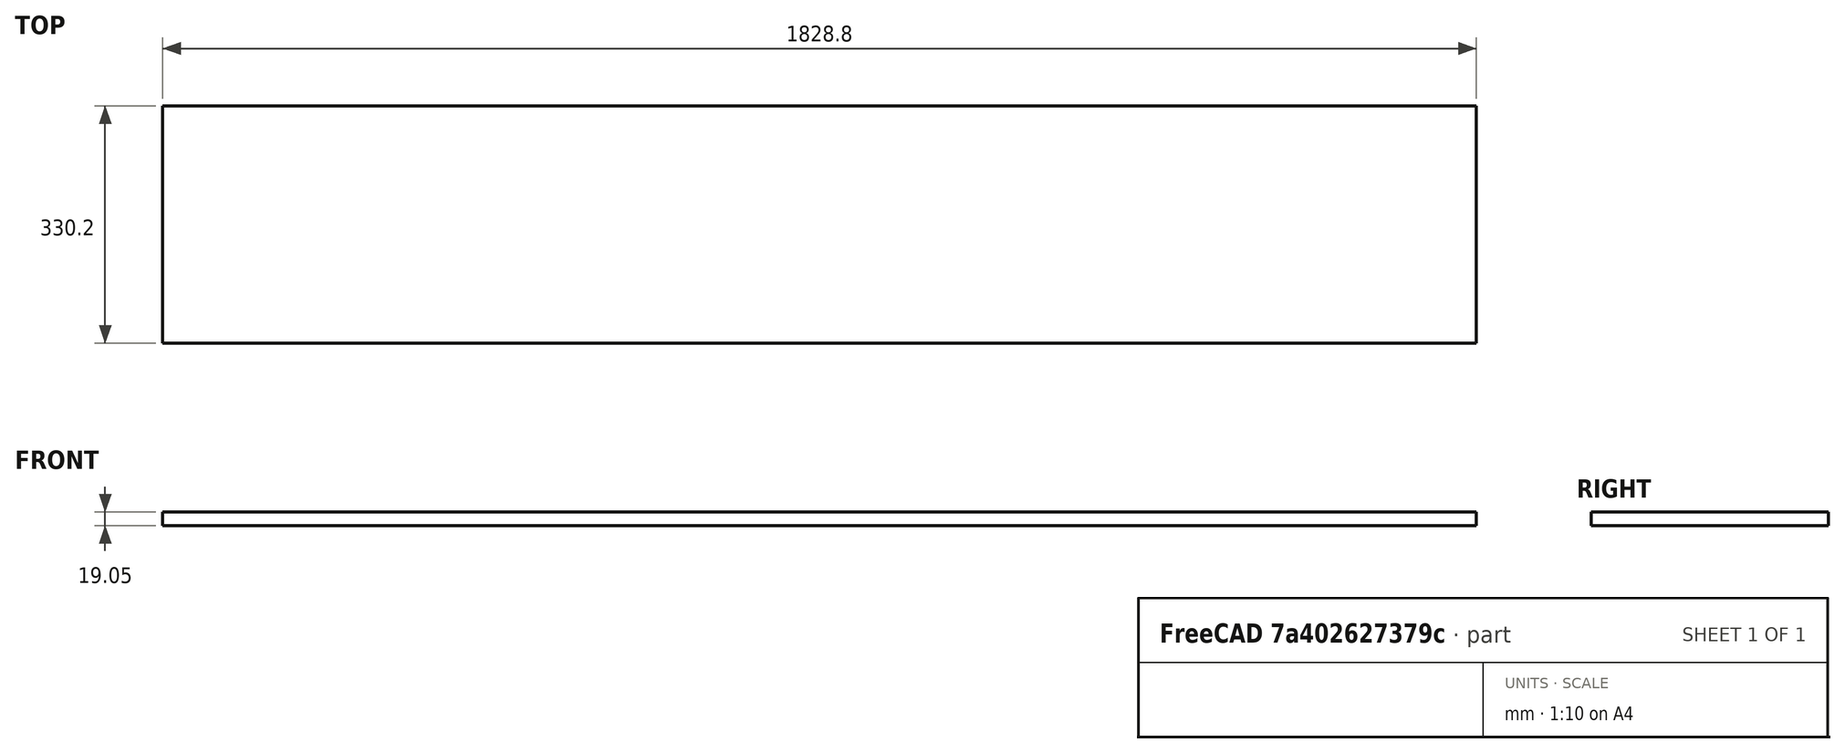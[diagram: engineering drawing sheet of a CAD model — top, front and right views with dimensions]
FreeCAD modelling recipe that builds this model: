
FCSTD DOCUMENT  (FreeCAD 0.15R4671 (Git))
Label: wb_bottom_rack_top
License: All rights reserved
LicenseURL: http://en.wikipedia.org/wiki/All_rights_reserved
objects: Sketcher::SketchObject×1, Part::Extrusion×1
note: 2 computed .brp shape members not serialized (recipe doc carries the construction recipe); baked Part::Feature solids carry a one-line shape summary decoded from their .brp

FEATURE [Sketcher::SketchObject] Sketch001
  sketch-geometry (4):
    g0: LineSegment StartX=0 StartY=0 StartZ=0 EndX=1828.8 EndY=0 EndZ=0
    g1: LineSegment StartX=1828.8 StartY=0 StartZ=0 EndX=1828.8 EndY=330.2 EndZ=0
    g2: LineSegment StartX=1828.8 StartY=330.2 StartZ=0 EndX=0 EndY=330.2 EndZ=0
    g3: LineSegment StartX=0 StartY=330.2 StartZ=0 EndX=0 EndY=0 EndZ=0
  constraints (11):
    c: Coincident(g0,g1)
    c: Coincident(g1,g2)
    c: Coincident(g2,g3)
    c: Coincident(g3,g0)
    c: Horizontal(g0)
    c: Horizontal(g2)
    c: Vertical(g1)
    c: Vertical(g3)
    c: Coincident(g0,g-1)
    c: Distance(g3) = 330.2
    c: Distance(g0) = 1828.8
FEATURE [Part::Extrusion] Extrude
  Base = -> Sketch001
  Dir = (0,0,19.05)
  Solid = true
